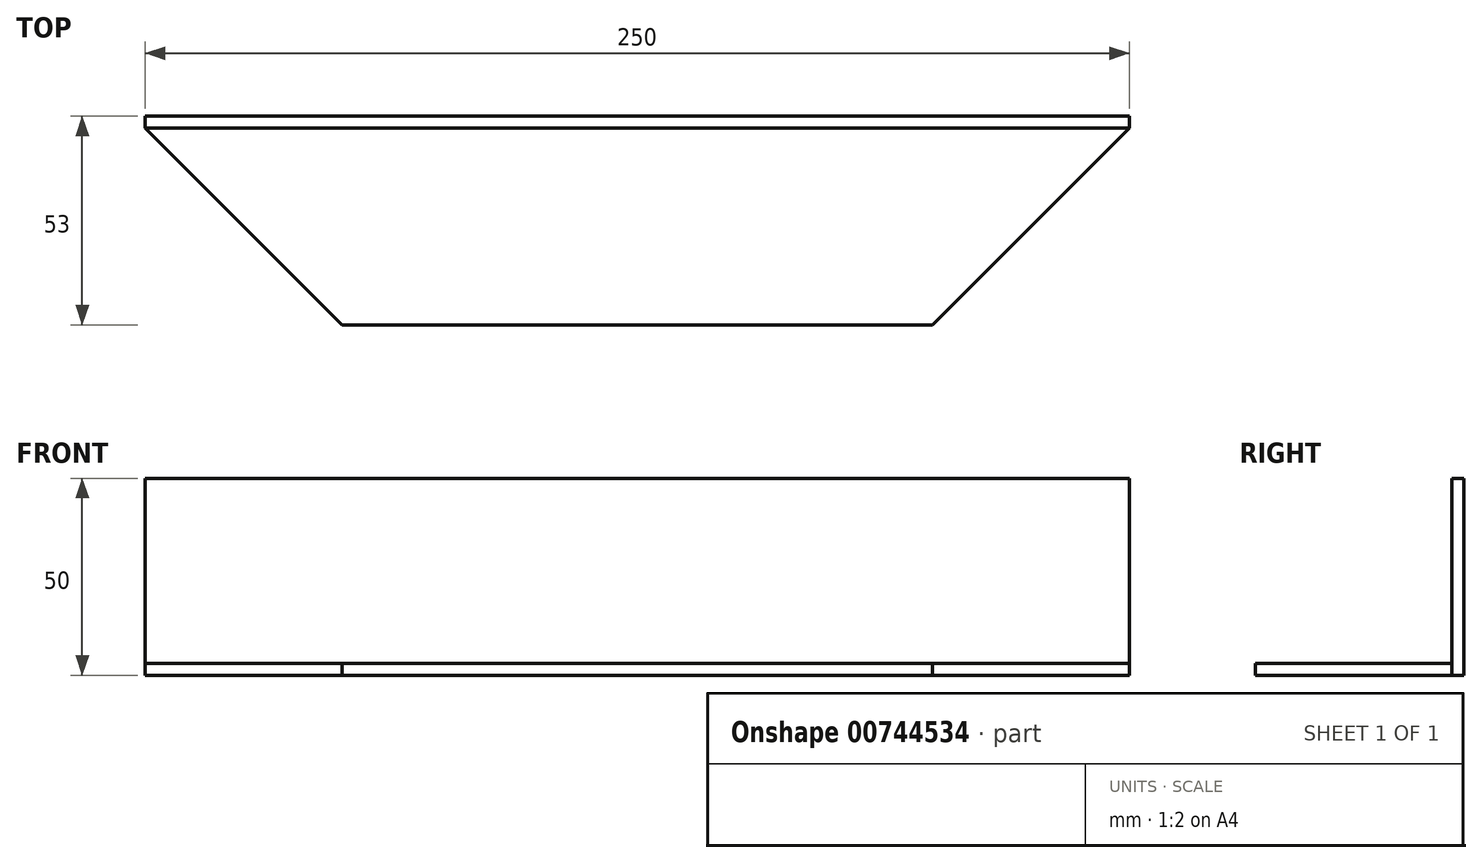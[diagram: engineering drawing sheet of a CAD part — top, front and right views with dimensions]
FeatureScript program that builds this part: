
annotation { "Feature Type Name" : "Feature", "Feature Type Description" : "" }
export const myFeature = defineFeature(function(context is Context, id is Id, definition is map)
    precondition{}
    {
        {
            var Q0;
            Q0=qCreatedBy(makeId("Top.planeOp"),FACE);
            var sketch = newSketch(context, id + "F0", { "sketchPlane" : qUnion([Q0])});
            skLineSegment(sketch, "E0.bottom", {"start": v(-127.46, 200) * mm, "end": v(122.54, 200) * mm});
            skLineSegment(sketch, "E1.bottom", {"start": v(-77.46, 150) * mm, "end": v(72.54, 150) * mm});
            skLineSegment(sketch, "E2", {"start": v(-127.46, 200) * mm, "end": v(-41.79, 200) * mm});
            skLineSegment(sketch, "E3", {"start": v(-77.46, 150) * mm, "end": v(-127.46, 200) * mm});
            skLineSegment(sketch, "E4", {"start": v(72.54, 150) * mm, "end": v(122.54, 200) * mm});
            skLineSegment(sketch, "E5", {"start": v(122.54, 200) * mm, "end": v(122.54, 203) * mm});
            skLineSegment(sketch, "E6", {"start": v(-127.46, 200) * mm, "end": v(-127.46, 203) * mm});
            skLineSegment(sketch, "E7", {"start": v(-127.46, 203) * mm, "end": v(122.54, 203) * mm});
            skSolve(sketch);
        }
        {
            var Q0;
            Q0=makeQuery(id+"F0.imprint","IMPRINT",FACE,{"disambiguationData":[TD([[makeQuery(id+"F0.imprint","IMPRINT",EDGE,{"derivedFrom":sQuery(id+"F0.wireOp",EDGE,"E0.bottom")}),1.0]])]});
            extrude(context, id + "F1", {"entities" : qUnion([Q0]), "depth" : 50 * mm, "offsetDistance" : 25 * mm});
        }
        {
            var Q0;
            Q0=makeQuery(id+"F0.imprint","IMPRINT",FACE,{"disambiguationData":[TD([[makeQuery(id+"F0.imprint","IMPRINT",EDGE,{"derivedFrom":sQuery(id+"F0.wireOp",EDGE,"E0.bottom")}),-1.0]])]});
            extrude(context, id + "F2", {"entities" : qUnion([Q0]), "operationType" : NewBodyOperationType.ADD, "depth" : 3 * mm, "offsetDistance" : 25 * mm});
        }
    });
